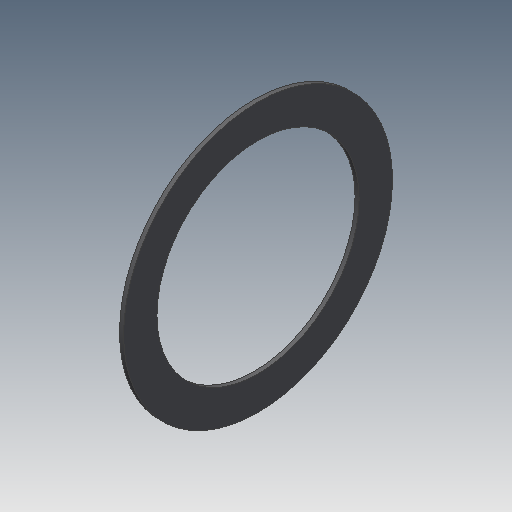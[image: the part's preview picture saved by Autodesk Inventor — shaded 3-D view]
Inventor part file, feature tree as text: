
AUTODESK INVENTOR PART (.ipt)
format: ipt  version: 2019.4 (Build 234330000, 330)  size: 102,912 bytes
history: native  units: mm
features: other x7, revolve x1, sketch x1
ambient origin geometry x8: Origin, YZ Plane, XZ Plane, XY Plane, X Axis, Y Axis, Z Axis, Center Point
bodies: Solid1 (feature_tree)
feature tree (9):
  revolve  "Revolution1"  [1 undecoded]
  other  "ip_st_1_XY"
  other  "ip_st_1_YZ"
  other  "ip_st_1_ZX"
  other  "ip_st_1_X"
  other  "ip_st_1_Y"
  other  "ip_st_1_Z"
  other  "ip_st_1_Center"
  sketch  "Sketch_1"  dims[d0=360.0deg d1=0.0mm]
note: 1 required parameter value undecoded (feature->parameter linkage not recoverable at this tier; creation-order binding heuristic only, values carry confidence <= 0.55)
